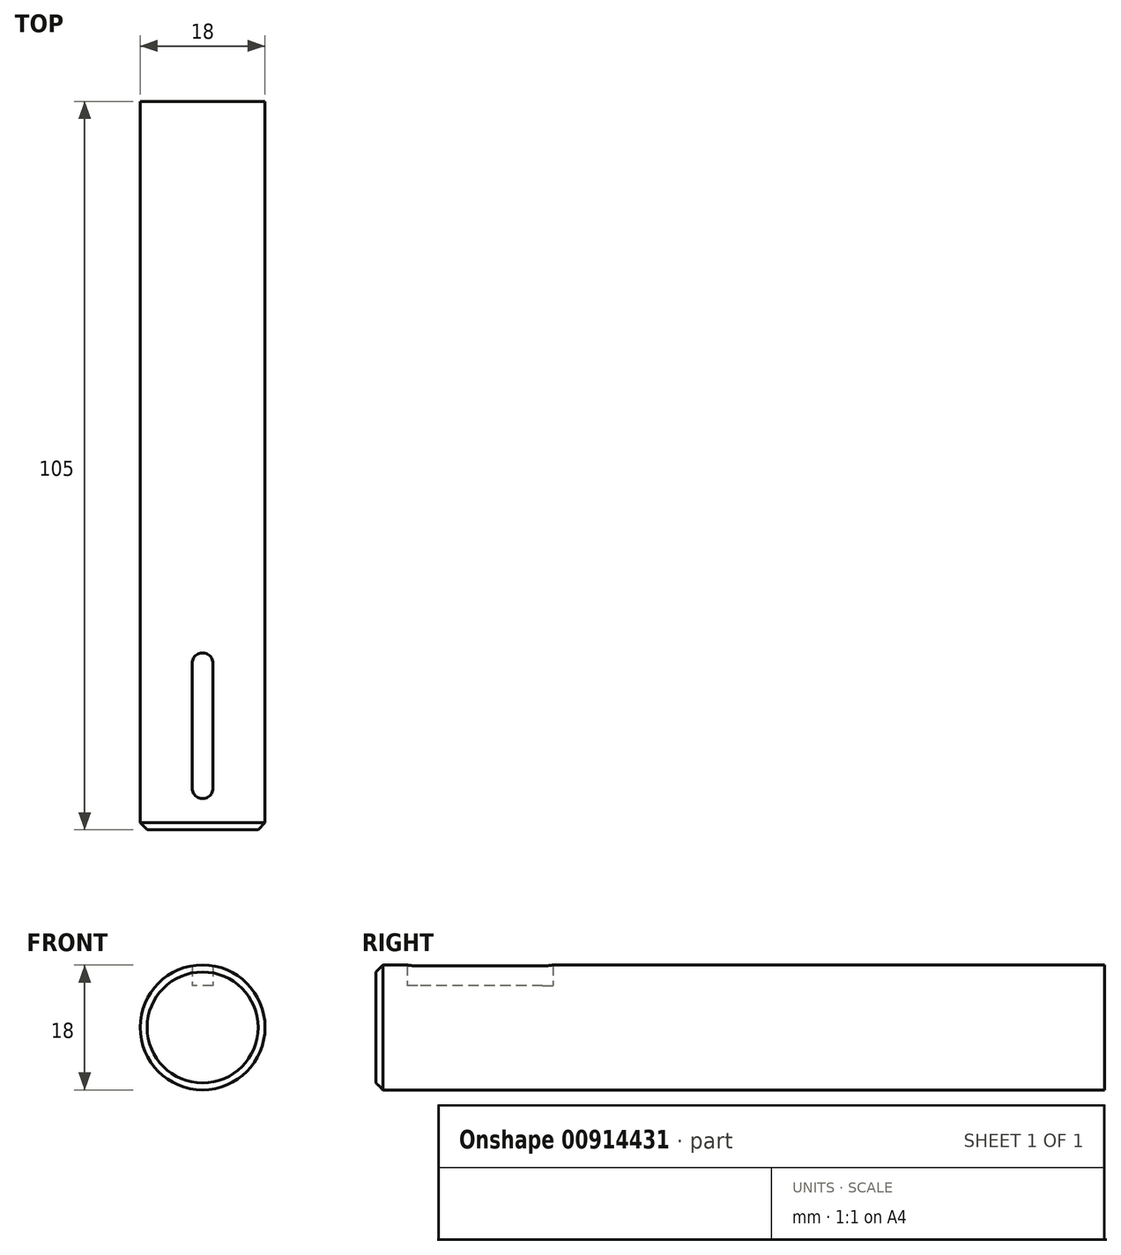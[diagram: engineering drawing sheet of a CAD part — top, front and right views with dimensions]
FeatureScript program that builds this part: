
annotation { "Feature Type Name" : "Feature", "Feature Type Description" : "" }
export const myFeature = defineFeature(function(context is Context, id is Id, definition is map)
    precondition{}
    {
        {
            var Q0;
            Q0=qCreatedBy(makeId("Front.planeOp"),FACE);
            var sketch = newSketch(context, id + "F0", { "sketchPlane" : qUnion([Q0])});
            skCircle(sketch, "E0", {"center": v(0, 0) * mm, "radius": 9 * mm});
            skSolve(sketch);
        }
        {
            var Q0;
            Q0 = qSketchRegion(id + "F0", true);
            extrude(context, id + "F1", {"entities" : qUnion([Q0]), "depth" : 105 * mm, "offsetDistance" : 25 * mm});
        }
        {
            var Q0;
            Q0=makeQuery(id+"F1.opExtrude","CAP_FACE",FACE,{"disambiguationData":[OSD([sQuery(id+"F0.wireOp",EDGE,"E0")])],"isStart":false});
            chamfer(context, id + "F2", {"entities" : qUnion([Q0]), "width" : 1 * mm, "tangentPropagation" : true});
        }
        {
            var Q0;
            Q0=qCreatedBy(makeId("Top.planeOp"),FACE);
            cPlane(context, id + "F3", {"entities" : qUnion([Q0]), "cplaneType" : CPlaneType.OFFSET, "offset" : 6 * mm, "width" : 150 * mm, "height" : 150 * mm});
        }
        {
            var Q0;
            Q0=qCreatedBy(id+"F3.planeOp",FACE);
            var sketch = newSketch(context, id + "F4", { "sketchPlane" : qUnion([Q0])});
            skLineSegment(sketch, "E1", {"start": v(0, -81) * mm, "end": v(0, -99) * mm});
            skArc(sketch, "E2.0.startCap", {"start": v(-1.5, -81) * mm, "mid": v(0, -79.5) * mm, "end": v(1.5, -81) * mm});
            skArc(sketch, "E2.0.endCap", {"start": v(1.5, -99) * mm, "mid": v(0, -100.5) * mm, "end": v(-1.5, -99) * mm});
            skLineSegment(sketch, "E2.0.left", {"start": v(1.5, -81) * mm, "end": v(1.5, -99) * mm});
            skLineSegment(sketch, "E2.0.right", {"start": v(-1.5, -81) * mm, "end": v(-1.5, -99) * mm});
            skSolve(sketch);
        }
        {
            var Q0;
            Q0 = qSketchRegion(id + "F4", true);
            extrude(context, id + "F5", {"entities" : qUnion([Q0]), "operationType" : NewBodyOperationType.REMOVE, "depth" : 25 * mm, "offsetDistance" : 25 * mm});
        }
    });
